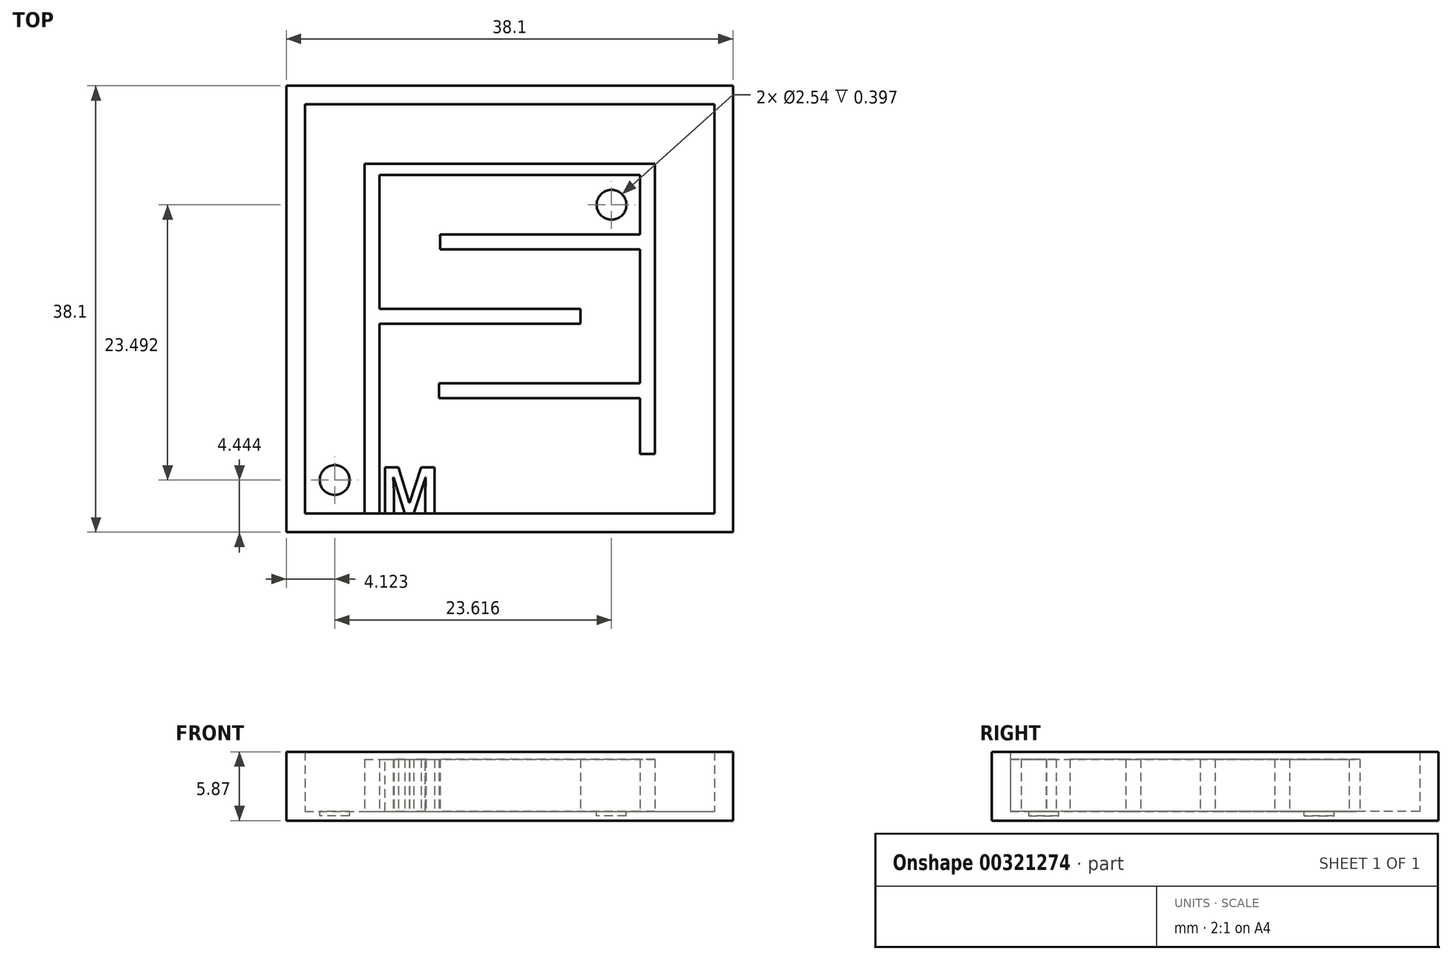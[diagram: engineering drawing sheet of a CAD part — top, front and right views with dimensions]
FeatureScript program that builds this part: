
annotation { "Feature Type Name" : "Feature", "Feature Type Description" : "" }
export const myFeature = defineFeature(function(context is Context, id is Id, definition is map)
    precondition{}
    {
        {
            var Q0;
            Q0=qCreatedBy(makeId("Top.planeOp"),FACE);
            var sketch = newSketch(context, id + "F0", { "sketchPlane" : qUnion([Q0])});
            skLineSegment(sketch, "E0.bottom", {"start": v(-14.46, 17) * mm, "end": v(23.64, 17) * mm});
            skLineSegment(sketch, "E0.top", {"start": v(-14.46, -21.1) * mm, "end": v(23.64, -21.1) * mm});
            skLineSegment(sketch, "E0.left", {"start": v(-14.46, 17) * mm, "end": v(-14.46, -21.1) * mm});
            skLineSegment(sketch, "E0.right", {"start": v(23.64, 17) * mm, "end": v(23.64, -21.1) * mm});
            skSolve(sketch);
        }
        {
            var Q0;
            Q0=makeQuery(id+"F0.imprint","IMPRINT",FACE,{"disambiguationData":[TD([[makeQuery(id+"F0.imprint","IMPRINT",EDGE,{"derivedFrom":sQuery(id+"F0.wireOp",EDGE,"E0.bottom")}),-1.0]])]});
            extrude(context, id + "F1", {"entities" : qUnion([Q0]), "depth" : 0.8 * mm});
        }
        {
            var Q0;
            Q0=makeQuery(id+"F1.opExtrude","CAP_FACE",FACE,{"disambiguationData":[OSD([sQuery(id+"F0.wireOp",EDGE,"E0.bottom"),sQuery(id+"F0.wireOp",EDGE,"E0.top"),sQuery(id+"F0.wireOp",EDGE,"E0.left"),sQuery(id+"F0.wireOp",EDGE,"E0.right")])],"isStart":false});
            var sketch = newSketch(context, id + "F2", { "sketchPlane" : qUnion([Q0])});
            skLineSegment(sketch, "E1.0", {"start": v(-12.88, 15.4) * mm, "end": v(22.05, 15.4) * mm});
            skLineSegment(sketch, "E1.1", {"start": v(-12.88, 15.4) * mm, "end": v(-12.88, -19.52) * mm});
            skLineSegment(sketch, "E1.2", {"start": v(-12.88, -19.52) * mm, "end": v(22.05, -19.52) * mm});
            skLineSegment(sketch, "E1.3", {"start": v(22.05, 15.4) * mm, "end": v(22.05, -19.52) * mm});
            skSolve(sketch);
        }
        {
            var Q0;
            Q0=makeQuery(id+"F2.imprint","IMPRINT",FACE,{"disambiguationData":[TD([[makeQuery(id+"F2.imprint","IMPRINT",EDGE,{"derivedFrom":sQuery(id+"F2.wireOp",EDGE,"E1.0")}),1.0]])]});
            extrude(context, id + "F3", {"entities" : qUnion([Q0]), "operationType" : NewBodyOperationType.ADD, "depth" : 5.08 * mm});
        }
        {
            var Q0;
            Q0=makeQuery(id+"F1.opExtrude","CAP_FACE",FACE,{"disambiguationData":[OSD([sQuery(id+"F0.wireOp",EDGE,"E0.bottom"),sQuery(id+"F0.wireOp",EDGE,"E0.top"),sQuery(id+"F0.wireOp",EDGE,"E0.left"),sQuery(id+"F0.wireOp",EDGE,"E0.right")])],"isStart":false});
            var sketch = newSketch(context, id + "F4", { "sketchPlane" : qUnion([Q0])});
            skLineSegment(sketch, "E2.bottom", {"start": v(-7.8, -19.52) * mm, "end": v(-6.53, -19.52) * mm});
            skLineSegment(sketch, "E2.top", {"start": v(-7.8, 10.33) * mm, "end": v(-6.53, 10.33) * mm});
            skLineSegment(sketch, "E2.left", {"start": v(-7.8, -19.52) * mm, "end": v(-7.8, 10.33) * mm});
            skLineSegment(sketch, "E2.right", {"start": v(-6.53, -19.52) * mm, "end": v(-6.53, 9.38) * mm});
            skLineSegment(sketch, "E3.top", {"start": v(-6.53, 9.38) * mm, "end": v(15.7, 9.38) * mm});
            skPoint(sketch, "E4.oppositeSnap0", {"position": v(15.7, 3.98) * mm});
            skLineSegment(sketch, "E5.top", {"start": v(16.97, -14.44) * mm, "end": v(15.7, -14.44) * mm});
            skLineSegment(sketch, "E5.left", {"start": v(16.97, 9.38) * mm, "end": v(16.97, -14.44) * mm});
            skLineSegment(sketch, "E5.right", {"start": v(15.7, 9.06) * mm, "end": v(15.7, -14.44) * mm});
            skLineSegment(sketch, "E6.bottom", {"start": v(15.7, -9.67) * mm, "end": v(-1.45, -9.67) * mm});
            skLineSegment(sketch, "E6.top", {"start": v(15.7, -8.4) * mm, "end": v(-1.45, -8.4) * mm});
            skLineSegment(sketch, "E6.left", {"start": v(15.7, -9.67) * mm, "end": v(15.7, -8.4) * mm});
            skLineSegment(sketch, "E6.right", {"start": v(-1.45, -9.67) * mm, "end": v(-1.45, -8.4) * mm});
            skPoint(sketch, "E7.firstSnap0", {"position": v(-12.88, -2.05) * mm});
            skLineSegment(sketch, "E7.bottom", {"start": v(-6.53, -2.05) * mm, "end": v(10.62, -2.05) * mm});
            skLineSegment(sketch, "E7.top", {"start": v(-6.53, -3.32) * mm, "end": v(10.62, -3.32) * mm});
            skLineSegment(sketch, "E7.left", {"start": v(-6.53, -2.05) * mm, "end": v(-6.53, -3.32) * mm});
            skLineSegment(sketch, "E7.right", {"start": v(10.62, -2.05) * mm, "end": v(10.62, -3.32) * mm});
            skLineSegment(sketch, "E8.bottom", {"start": v(15.7, 4.3) * mm, "end": v(-1.35, 4.3) * mm});
            skLineSegment(sketch, "E8.top", {"start": v(15.7, 3.03) * mm, "end": v(-1.35, 3.03) * mm});
            skLineSegment(sketch, "E8.left", {"start": v(15.7, 4.3) * mm, "end": v(15.7, 3.03) * mm});
            skLineSegment(sketch, "E8.right", {"start": v(-1.35, 4.3) * mm, "end": v(-1.35, 3.03) * mm});
            skLineSegment(sketch, "E9", {"start": v(-6.53, 10.33) * mm, "end": v(16.97, 10.33) * mm});
            skLineSegment(sketch, "E10", {"start": v(16.97, 10.33) * mm, "end": v(16.97, 9.38) * mm});
            skLineSegment(sketch, "E11", {"start": v(-12.88, -19.52) * mm, "end": v(-7.8, -19.52) * mm});
            skCircle(sketch, "E12", {"center": v(-10.34, -16.66) * mm, "radius": 1.27 * mm});
            skPoint(sketch, "E12.centerSnap0", {"position": v(-10.34, -19.52) * mm});
            skLineSegment(sketch, "E13", {"start": v(15.7, 9.06) * mm, "end": v(15.7, 9.38) * mm});
            skLineSegment(sketch, "E14", {"start": v(15.7, 9.38) * mm, "end": v(15.7, 4.3) * mm});
            skCircle(sketch, "E15", {"center": v(13.28, 6.84) * mm, "radius": 1.27 * mm});
            skPoint(sketch, "E15.centerSnap0", {"position": v(15.7, 6.84) * mm});
            skSolve(sketch);
        }
        {
            var Q0;
            Q0=makeQuery(id+"F4.imprint","IMPRINT",FACE,{"disambiguationData":[TD([[makeQuery(id+"F4.imprint","IMPRINT",EDGE,{"derivedFrom":sQuery(id+"F4.wireOp",EDGE,"E12")}),1.0]])]});
            var Q1;
            Q1=makeQuery(id+"F4.imprint","IMPRINT",FACE,{"disambiguationData":[TD([[makeQuery(id+"F4.imprint","IMPRINT",EDGE,{"derivedFrom":sQuery(id+"F4.wireOp",EDGE,"E15")}),1.0]])]});
            extrude(context, id + "F5", {"entities" : qUnion([Q0, Q1]), "operationType" : NewBodyOperationType.REMOVE, "oppositeDirection" : true, "depth" : 0.4 * mm});
        }
        {
            var Q0;
            {var subQ7=sQuery(id+"F4.wireOp",EDGE,"E2.bottom");Q0=makeQuery(id+"F4.imprint","IMPRINT",FACE,{"disambiguationData":[TD([[makeQuery(id+"F4.imprint","IMPRINT",EDGE,{"derivedFrom":subQ7}),1.0]])]});}
            var Q1;
            Q1=makeQuery(id+"F4.imprint","IMPRINT",FACE,{"disambiguationData":[TD([[makeQuery(id+"F4.imprint","IMPRINT",EDGE,{"derivedFrom":sQuery(id+"F4.wireOp",EDGE,"E8.bottom")}),1.0]])]});
            var Q2;
            Q2=makeQuery(id+"F4.imprint","IMPRINT",FACE,{"disambiguationData":[TD([[makeQuery(id+"F4.imprint","IMPRINT",EDGE,{"derivedFrom":sQuery(id+"F4.wireOp",EDGE,"E7.bottom")}),-1.0]])]});
            var Q3;
            Q3=makeQuery(id+"F4.imprint","IMPRINT",FACE,{"disambiguationData":[TD([[makeQuery(id+"F4.imprint","IMPRINT",EDGE,{"derivedFrom":sQuery(id+"F4.wireOp",EDGE,"E6.bottom")}),-1.0]])]});
            extrude(context, id + "F6", {"entities" : qUnion([Q0, Q1, Q2, Q3]), "operationType" : NewBodyOperationType.ADD, "depth" : 4.44 * mm});
        }
        {
            var Q0;
            Q0=makeQuery(id+"F1.opExtrude","CAP_FACE",FACE,{"disambiguationData":[OSD([sQuery(id+"F0.wireOp",EDGE,"E0.bottom"),sQuery(id+"F0.wireOp",EDGE,"E0.top"),sQuery(id+"F0.wireOp",EDGE,"E0.left"),sQuery(id+"F0.wireOp",EDGE,"E0.right")])],"isStart":false});
            var sketch = newSketch(context, id + "F7", { "sketchPlane" : qUnion([Q0])});
            skText(sketch, "E16", { "text": "M", "fontName": "OpenSans-Bold.ttf"});
            const initialGuessF7  = {"E16": [-0.00653, -0.01952, 1, 0, 0.00397]};
            skSetInitialGuess(sketch, initialGuessF7);
            skSolve(sketch);
        }
        {
            var Q0;
            Q0 = qSketchRegion(id + "F7", true);
            extrude(context, id + "F8", {"entities" : qUnion([Q0]), "operationType" : NewBodyOperationType.ADD, "depth" : 4.44 * mm});
        }
    });
